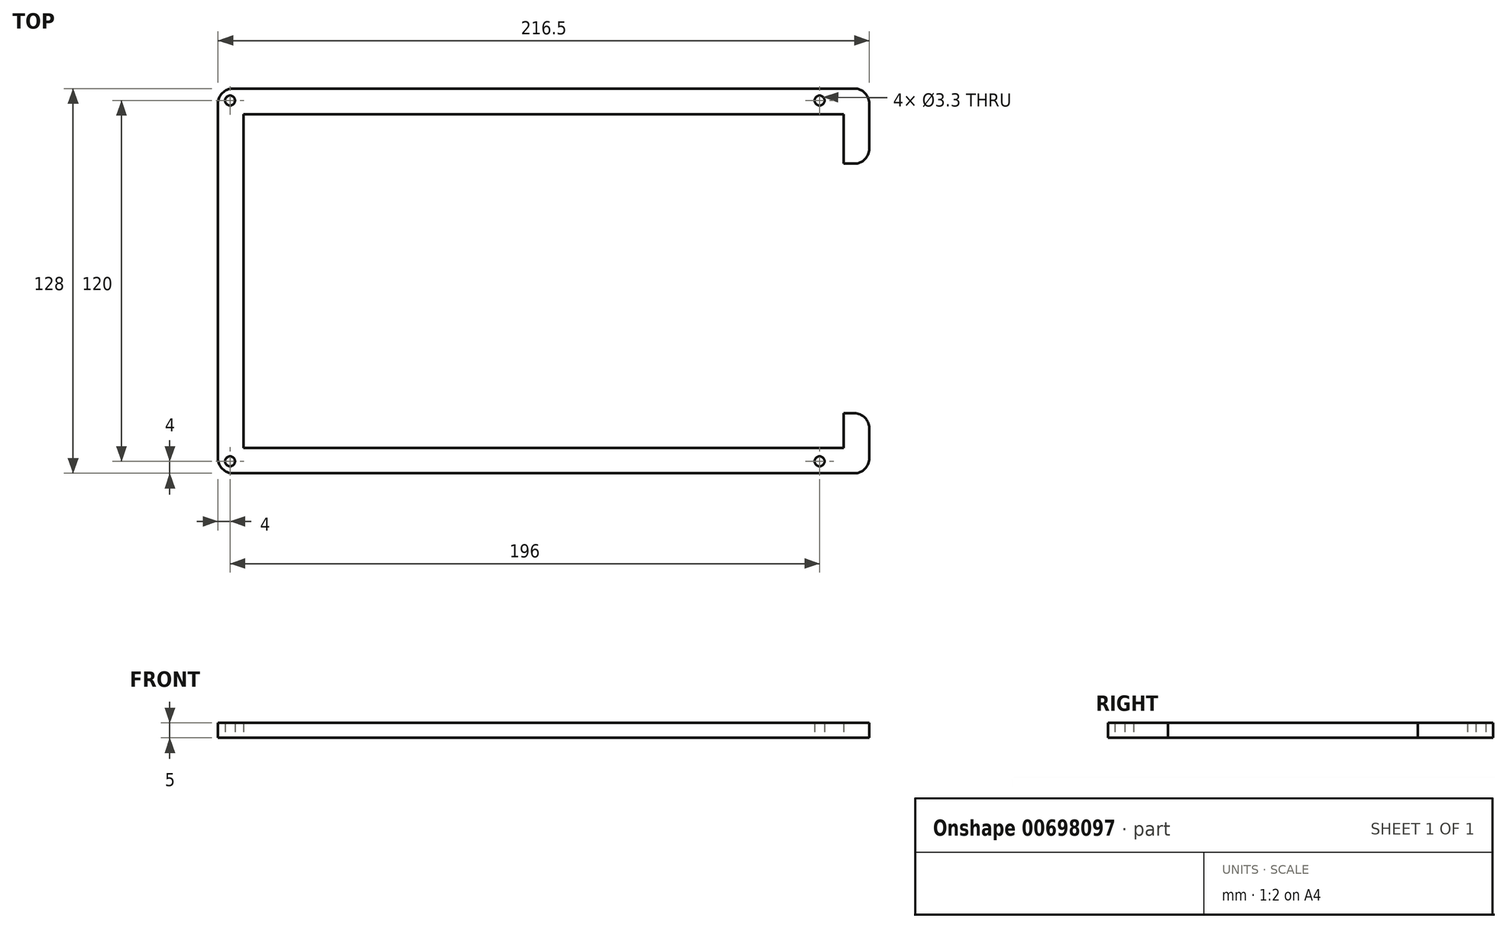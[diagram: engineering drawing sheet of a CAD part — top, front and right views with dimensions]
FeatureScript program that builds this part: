
annotation { "Feature Type Name" : "Feature", "Feature Type Description" : "" }
export const myFeature = defineFeature(function(context is Context, id is Id, definition is map)
    precondition{}
    {
        {
            var Q0;
            Q0=qCreatedBy(makeId("Top.planeOp"),FACE);
            var sketch = newSketch(context, id + "F0", { "sketchPlane" : qUnion([Q0])});
            skLineSegment(sketch, "E0.bottom", {"start": v(83, 50.5) * mm, "end": v(-83, 50.5) * mm});
            skLineSegment(sketch, "E0.top", {"start": v(83, -50.5) * mm, "end": v(-83, -50.5) * mm});
            skLineSegment(sketch, "E0.left", {"start": v(83, 50.5) * mm, "end": v(83, -50.5) * mm});
            skLineSegment(sketch, "E0.right", {"start": v(-83, 50.5) * mm, "end": v(-83, -50.5) * mm});
            skPoint(sketch, "E0.middle", {"position": v(0, 0) * mm});
            skLineSegment(sketch, "E1.0", {"start": v(-91, 54.5) * mm, "end": v(-91, -53.5) * mm, "construction": true});
            skLineSegment(sketch, "E1.1", {"start": v(93, 54.5) * mm, "end": v(-91, 54.5) * mm, "construction": true});
            skLineSegment(sketch, "E1.2", {"start": v(93, 54.5) * mm, "end": v(93, -53.5) * mm, "construction": true});
            skLineSegment(sketch, "E1.3", {"start": v(93, -53.5) * mm, "end": v(-91, -53.5) * mm, "construction": true});
            skLineSegment(sketch, "E2.0", {"start": v(103, 64.5) * mm, "end": v(-101, 64.5) * mm});
            skLineSegment(sketch, "E2.2", {"start": v(103, -63.5) * mm, "end": v(-101, -63.5) * mm});
            skLineSegment(sketch, "E2.3", {"start": v(-101, 64.5) * mm, "end": v(-101, -63.5) * mm});
            skLineSegment(sketch, "E3.0", {"start": v(99, 60.5) * mm, "end": v(-97, 60.5) * mm, "construction": true});
            skLineSegment(sketch, "E3.1", {"start": v(99, 60.5) * mm, "end": v(99, -59.5) * mm, "construction": true});
            skLineSegment(sketch, "E3.2", {"start": v(99, -59.5) * mm, "end": v(-97, -59.5) * mm, "construction": true});
            skLineSegment(sketch, "E3.3", {"start": v(-97, 60.5) * mm, "end": v(-97, -59.5) * mm, "construction": true});
            skLineSegment(sketch, "E4", {"start": v(103, 64.5) * mm, "end": v(115.5, 64.5) * mm});
            skLineSegment(sketch, "E5", {"start": v(115.5, -63.5) * mm, "end": v(103, -63.5) * mm});
            skLineSegment(sketch, "E6", {"start": v(115.5, 64.5) * mm, "end": v(115.5, 39.5) * mm});
            skPoint(sketch, "E7.orphan", {"position": v(133, -63.5) * mm});
            skLineSegment(sketch, "E8.0", {"start": v(103, 56) * mm, "end": v(107, 56) * mm});
            skLineSegment(sketch, "E8.1", {"start": v(-92.5, 56) * mm, "end": v(-92.5, -55) * mm});
            skLineSegment(sketch, "E8.2", {"start": v(103, -55) * mm, "end": v(-92.5, -55) * mm});
            skLineSegment(sketch, "E8.3", {"start": v(103, 56) * mm, "end": v(-92.5, 56) * mm});
            skLineSegment(sketch, "E8.4", {"start": v(107, -55) * mm, "end": v(103, -55) * mm});
            skLineSegment(sketch, "E8.5", {"start": v(107, 56) * mm, "end": v(107, 39.5) * mm});
            skLineSegment(sketch, "E9", {"start": v(107, -43.5) * mm, "end": v(115.5, -43.5) * mm});
            skLineSegment(sketch, "E10", {"start": v(107, 39.5) * mm, "end": v(115.5, 39.5) * mm});
            skLineSegment(sketch, "E11.trimOffspring", {"start": v(107, -43.5) * mm, "end": v(107, -55) * mm});
            skLineSegment(sketch, "E12.trimOffspring", {"start": v(115.5, -43.5) * mm, "end": v(115.5, -63.5) * mm});
            skSolve(sketch);
        }
        {
            var Q0;
            Q0=makeQuery(id+"F0.imprint","IMPRINT",FACE,{"disambiguationData":[TD([[makeQuery(id+"F0.imprint","IMPRINT",EDGE,{"derivedFrom":sQuery(id+"F0.wireOp",EDGE,"E2.0")}),1.0]])]});
            extrude(context, id + "F1", {"entities" : qUnion([Q0]), "depth" : 5 * mm, "offsetDistance" : 25 * mm});
        }
        {
            var Q0;
            Q0=sQuery(id+"F0.wireOp",VERTEX,"E3.0.end");
            var Q1;
            Q1=sQuery(id+"F0.wireOp",VERTEX,"E3.0.start");
            var Q2;
            Q2=sQuery(id+"F0.wireOp",VERTEX,"E3.1.end");
            var Q3;
            Q3=sQuery(id+"F0.wireOp",VERTEX,"E3.2.end");
            var Q4;
            Q4=makeQuery(id+"F1.opExtrude","SWEPT_BODY",BODY,{"disambiguationData":[OSD([sQuery(id+"F0.wireOp",EDGE,"E0.bottom"),sQuery(id+"F0.wireOp",EDGE,"E0.top"),sQuery(id+"F0.wireOp",EDGE,"E0.left"),sQuery(id+"F0.wireOp",EDGE,"E0.right"),sQuery(id+"F0.wireOp",EDGE,"E2.0"),sQuery(id+"F0.wireOp",EDGE,"E2.1"),sQuery(id+"F0.wireOp",EDGE,"E2.2"),sQuery(id+"F0.wireOp",EDGE,"E2.3")])]});
            hole(context, id + "F2", {"style" : HoleStyle.SIMPLE, "endStyle" : HoleEndStyle.THROUGH, "oppositeDirection" : true, "standardTappedOrClearance" : lookupTablePath({ "standard" : "ISO", "fit" : "Normal", "size" : "M3", "type" : "Clearance" }), "standardBlindInLast" : lookupTablePath({ "fit" : "Standard", "standard" : "ISO", "size" : "M3", "type" : "Clearance" }), "holeDiameter" : 3.3 * mm, "majorDiameter" : 5 * mm, "isTappedThrough" : true, "tappedDepth" : 12 * mm, "tapClearance" : 3, "startFromSketch" : true, "locations" : qUnion([Q0, Q1, Q2, Q3]), "scope" : qUnion([Q4])});
        }
        {
            var Q0;
            Q0=makeQuery(id+"F1.opExtrude","SWEPT_EDGE",EDGE,{"disambiguationData":[OSD([sQuery(id+"F0.wireOp",EDGE,"E6"),sQuery(id+"F0.wireOp",EDGE,"E10")])]});
            var Q1;
            Q1=makeQuery(id+"F1.opExtrude","SWEPT_EDGE",EDGE,{"disambiguationData":[OSD([sQuery(id+"F0.wireOp",EDGE,"E4"),sQuery(id+"F0.wireOp",EDGE,"E6")])]});
            var Q2;
            Q2=makeQuery(id+"F1.opExtrude","SWEPT_EDGE",EDGE,{"disambiguationData":[OSD([sQuery(id+"F0.wireOp",EDGE,"E2.0"),sQuery(id+"F0.wireOp",EDGE,"E2.3")])]});
            var Q3;
            Q3=makeQuery(id+"F1.opExtrude","SWEPT_EDGE",EDGE,{"disambiguationData":[OSD([sQuery(id+"F0.wireOp",EDGE,"E2.2"),sQuery(id+"F0.wireOp",EDGE,"E2.3")])]});
            var Q4;
            Q4=makeQuery(id+"F1.opExtrude","SWEPT_EDGE",EDGE,{"disambiguationData":[OSD([sQuery(id+"F0.wireOp",EDGE,"E5"),sQuery(id+"F0.wireOp",EDGE,"E12.trimOffspring")])]});
            var Q5;
            Q5=makeQuery(id+"F1.opExtrude","SWEPT_EDGE",EDGE,{"disambiguationData":[OSD([sQuery(id+"F0.wireOp",EDGE,"E9"),sQuery(id+"F0.wireOp",EDGE,"E12.trimOffspring")])]});
            fillet(context, id + "F3", {"entities" : qUnion([Q0, Q1, Q2, Q3, Q4, Q5]), "radius" : 5 * mm, "tangentPropagation" : true, "allowEdgeOverflow" : false});
        }
    });
